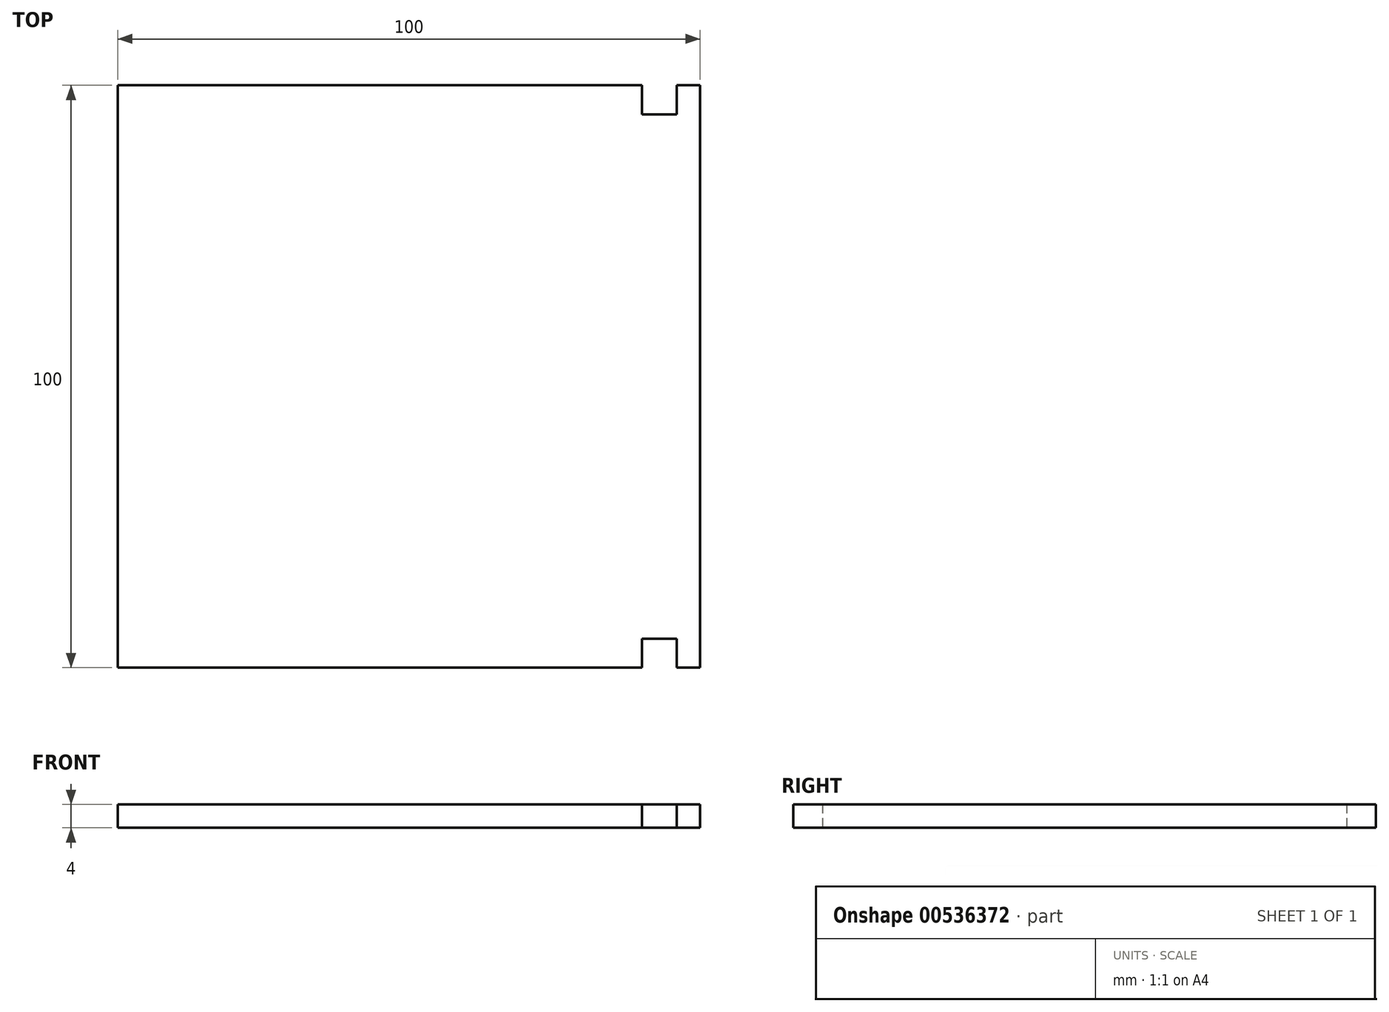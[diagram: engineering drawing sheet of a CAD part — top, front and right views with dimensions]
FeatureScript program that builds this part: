
annotation { "Feature Type Name" : "Feature", "Feature Type Description" : "" }
export const myFeature = defineFeature(function(context is Context, id is Id, definition is map)
    precondition{}
    {
        {
            var Q0;
            Q0=qCreatedBy(makeId("Top.planeOp"),FACE);
            var sketch = newSketch(context, id + "F0", { "sketchPlane" : qUnion([Q0])});
            skLineSegment(sketch, "E0.bottom", {"start": v(0, 0) * mm, "end": v(100, 0) * mm});
            skLineSegment(sketch, "E0.top", {"start": v(0, 100) * mm, "end": v(100, 100) * mm});
            skLineSegment(sketch, "E0.left", {"start": v(0, 0) * mm, "end": v(0, 100) * mm});
            skLineSegment(sketch, "E0.right", {"start": v(100, 0) * mm, "end": v(100, 100) * mm});
            skLineSegment(sketch, "E1.bottom", {"start": v(96, 0) * mm, "end": v(90, 0) * mm});
            skLineSegment(sketch, "E1.top", {"start": v(96, 5) * mm, "end": v(90, 5) * mm});
            skLineSegment(sketch, "E1.left", {"start": v(96, 0) * mm, "end": v(96, 5) * mm});
            skLineSegment(sketch, "E1.right", {"start": v(90, 0) * mm, "end": v(90, 5) * mm});
            skLineSegment(sketch, "E2.bottom", {"start": v(96, 100) * mm, "end": v(90, 100) * mm});
            skLineSegment(sketch, "E2.top", {"start": v(96, 95) * mm, "end": v(90, 95) * mm});
            skLineSegment(sketch, "E2.left", {"start": v(96, 100) * mm, "end": v(96, 95) * mm});
            skLineSegment(sketch, "E2.right", {"start": v(90, 100) * mm, "end": v(90, 95) * mm});
            skSolve(sketch);
        }
        {
            var Q0;
            {var subQ3=sQuery(id+"F0.wireOp",EDGE,"E0.left");Q0=makeQuery(id+"F0.imprint","IMPRINT",FACE,{"disambiguationData":[TD([[makeQuery(id+"F0.imprint","IMPRINT",EDGE,{"derivedFrom":subQ3}),-1.0]])]});}
            extrude(context, id + "F1", {"entities" : qUnion([Q0]), "depth" : 4 * mm, "offsetDistance" : 25 * mm});
        }
    });
